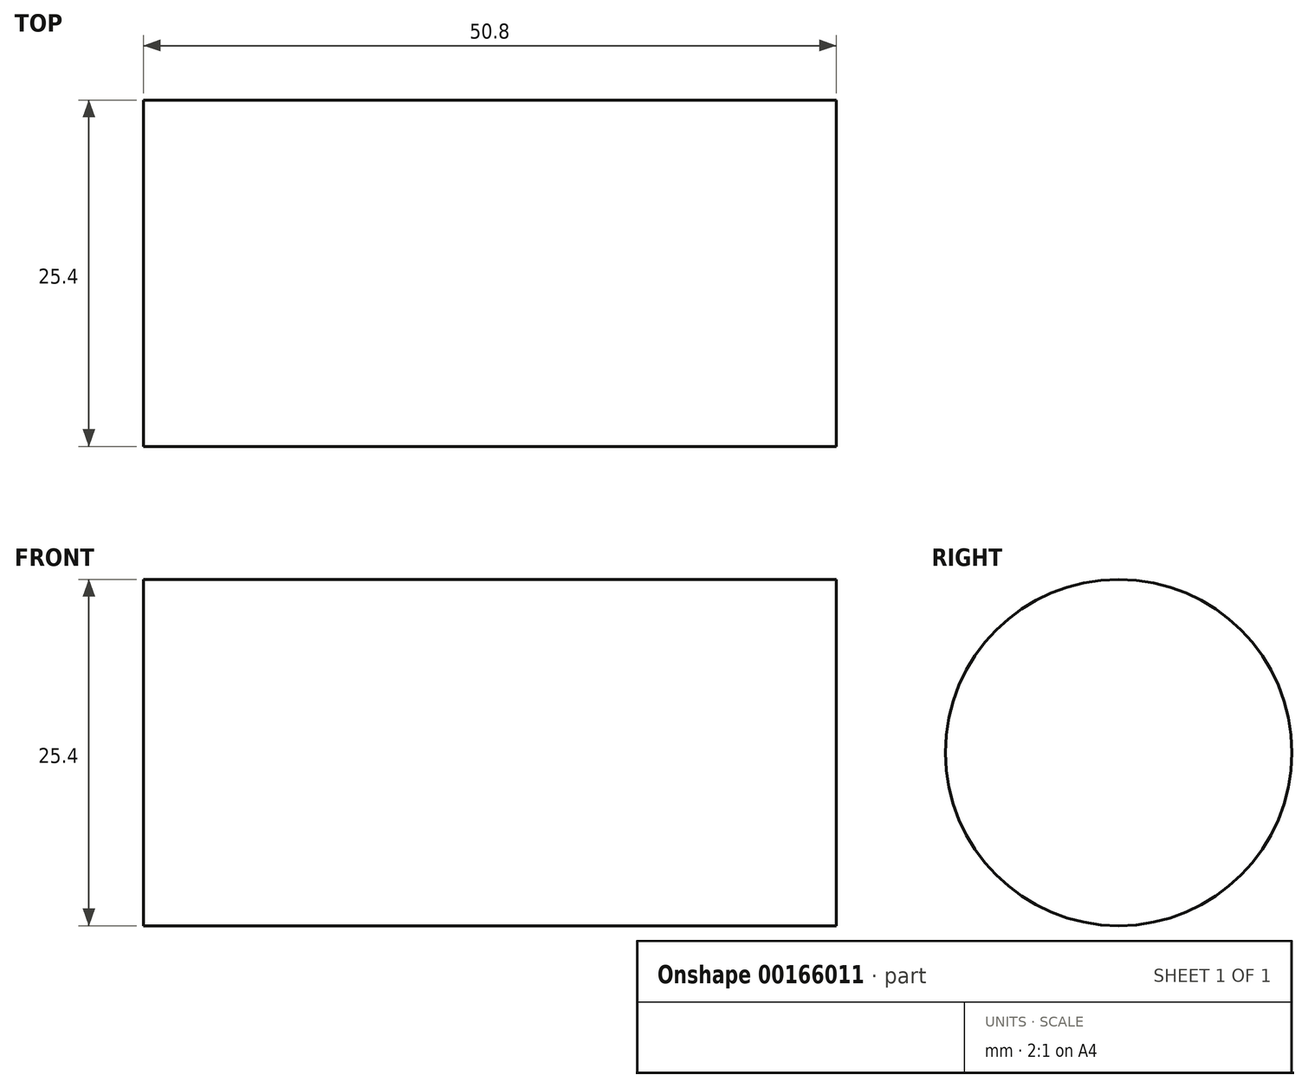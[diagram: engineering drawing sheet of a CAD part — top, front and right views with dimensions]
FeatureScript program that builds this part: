
annotation { "Feature Type Name" : "Feature", "Feature Type Description" : "" }
export const myFeature = defineFeature(function(context is Context, id is Id, definition is map)
    precondition{}
    {
        {
            var Q0;
            Q0=qCreatedBy(makeId("Right.planeOp"),FACE);
            var sketch = newSketch(context, id + "F0", { "sketchPlane" : qUnion([Q0])});
            skCircle(sketch, "E0", {"center": v(0, 0) * mm, "radius": 12.7 * mm});
            skSolve(sketch);
        }
        {
            var Q0;
            Q0 = qSketchRegion(id + "F0", true);
            extrude(context, id + "F1", {"entities" : qUnion([Q0]), "depth" : 50.8 * mm});
        }
        {
            var Q0;
            Q0=makeQuery(id+"F1.opExtrude","CAP_FACE",FACE,{"disambiguationData":[OSD([sQuery(id+"F0.wireOp",EDGE,"E0")])],"isStart":true});
            var sketch = newSketch(context, id + "F2", { "sketchPlane" : qUnion([Q0])});
            skLineSegment(sketch, "E1.bottom", {"start": v(-25.4, 3.18) * mm, "end": v(25.4, 3.18) * mm});
            skLineSegment(sketch, "E1.top", {"start": v(-25.4, -3.17) * mm, "end": v(25.4, -3.17) * mm});
            skLineSegment(sketch, "E1.left", {"start": v(-25.4, 3.18) * mm, "end": v(-25.4, -3.17) * mm});
            skLineSegment(sketch, "E1.right", {"start": v(25.4, 3.18) * mm, "end": v(25.4, -3.17) * mm});
            skPoint(sketch, "E1.middle", {"position": v(0, 0) * mm});
            skLineSegment(sketch, "E2.left", {"start": v(25.4, -3.17) * mm, "end": v(25.4, -3.17) * mm});
            skLineSegment(sketch, "E2.right", {"start": v(-25.4, -3.17) * mm, "end": v(-25.4, -3.17) * mm});
            skLineSegment(sketch, "E3.top", {"start": v(-25.4, 28.58) * mm, "end": v(25.4, 28.58) * mm});
            skLineSegment(sketch, "E3.left", {"start": v(-25.4, 3.18) * mm, "end": v(-25.4, 28.58) * mm});
            skLineSegment(sketch, "E3.right", {"start": v(25.4, 3.18) * mm, "end": v(25.4, 28.58) * mm});
            skLineSegment(sketch, "E4.bottom", {"start": v(25.4, -3.17) * mm, "end": v(-25.4, -3.17) * mm});
            skLineSegment(sketch, "E4.top", {"start": v(25.4, -53.98) * mm, "end": v(-25.4, -53.98) * mm});
            skLineSegment(sketch, "E4.left", {"start": v(25.4, -3.17) * mm, "end": v(25.4, -53.98) * mm});
            skLineSegment(sketch, "E4.right", {"start": v(-25.4, -3.17) * mm, "end": v(-25.4, -53.98) * mm});
            skSolve(sketch);
        }
        {
            var Q0;
            Q0=makeQuery(id+"F2.imprint","IMPRINT",FACE,{"disambiguationData":[TD([[makeQuery(id+"F2.imprint","IMPRINT",EDGE,{"derivedFrom":sQuery(id+"F2.wireOp",EDGE,"E3.top")}),-1.0]])]});
            var Q1;
            Q1=makeQuery(id+"F2.imprint","IMPRINT",FACE,{"disambiguationData":[TD([[makeQuery(id+"F2.imprint","IMPRINT",EDGE,{"derivedFrom":sQuery(id+"F2.wireOp",EDGE,"E4.top")}),-1.0]])]});
            extrude(context, id + "F3", {"entities" : qUnion([Q0, Q1]), "operationType" : NewBodyOperationType.REMOVE, "oppositeDirection" : true, "depth" : 25.4 * mm});
        }
    });
